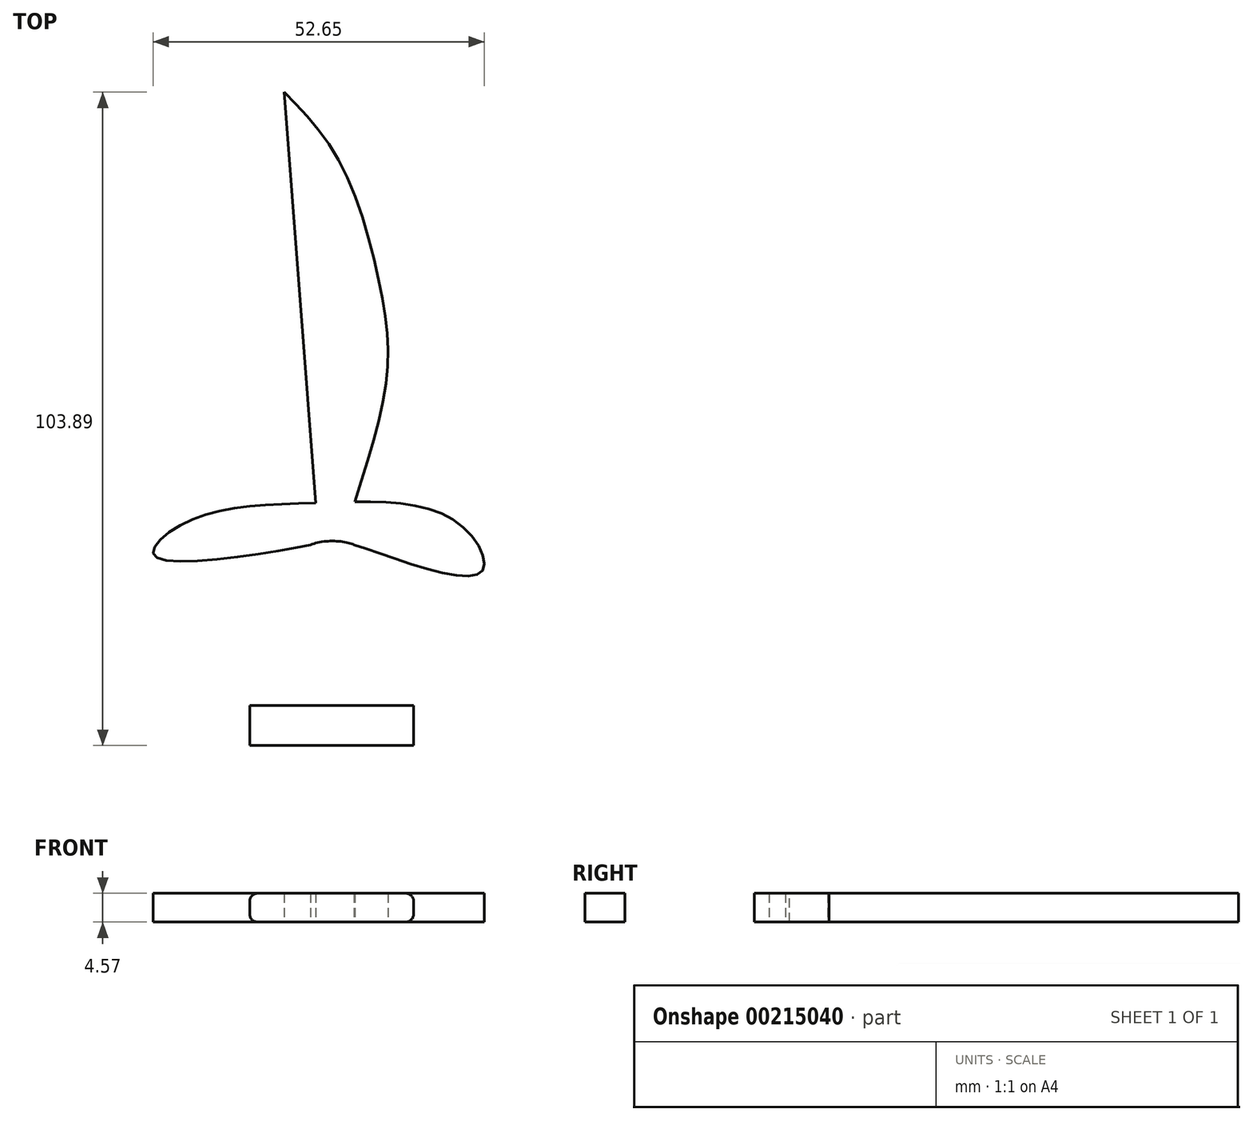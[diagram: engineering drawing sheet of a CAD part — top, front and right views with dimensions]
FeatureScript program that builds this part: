
annotation { "Feature Type Name" : "Feature", "Feature Type Description" : "" }
export const myFeature = defineFeature(function(context is Context, id is Id, definition is map)
    precondition{}
    {
        {
            var Q0;
            Q0=qCreatedBy(makeId("Top.planeOp"),FACE);
            var sketch = newSketch(context, id + "F0", { "sketchPlane" : qUnion([Q0])});
            skFitSpline(sketch, "E0", {"points": [v(-31.24, -28.4) * mm, v(-22.55, -28.4) * mm, v(-21.05, -21.21) * mm, v(-21.38, -5.85) * mm, v(-23.38, -3.34) * mm, v(-29.9, -3.5) * mm, v(-32.57, -9.02) * mm, v(-32.07, -26.22) * mm, v(-31.24, -28.4) * mm]});
            skFitSpline(sketch, "E1", {"points": [v(-29.06, 3.17) * mm, v(-49.94, 0) * mm, v(-54.62, -5.35) * mm, v(-29.9, -3.5) * mm, v(-22.97, -3.5) * mm, v(-3, -8.02) * mm, v(-6.51, 0) * mm, v(-29.06, 3.17) * mm]});
            skLineSegment(sketch, "E2.bottom", {"start": v(-13.53, -29.06) * mm, "end": v(-39.59, -29.06) * mm});
            skLineSegment(sketch, "E2.top", {"start": v(-13.53, -35.41) * mm, "end": v(-39.59, -35.41) * mm});
            skLineSegment(sketch, "E2.left", {"start": v(-13.53, -29.06) * mm, "end": v(-13.53, -35.41) * mm});
            skLineSegment(sketch, "E2.right", {"start": v(-39.59, -29.06) * mm, "end": v(-39.59, -35.41) * mm});
            skPoint(sketch, "E2.middle", {"position": v(-26.56, -32.24) * mm});
            skFitSpline(sketch, "E3", {"points": [v(-22.88, 3.37) * mm, v(-17.87, 22.55) * mm, v(-18.7, 36.75) * mm, v(-25.06, 56.96) * mm, v(-34.08, 68.48) * mm], "startDerivative": vector(24.14, 75.52) * mm, "endDerivative": vector(-42.27, 43.62) * mm});
            skLineSegment(sketch, "E4", {"start": v(-34.08, 68.48) * mm, "end": v(-29.06, 3.17) * mm});
            skSolve(sketch);
        }
        {
            var Q0;
            {var subQ0=sQuery(id+"F0.wireOp",EDGE,"E3");Q0=makeQuery(id+"F0.imprint","IMPRINT",FACE,{"disambiguationData":[TD([[makeQuery(id+"F0.imprint","IMPRINT",EDGE,{"derivedFrom":subQ0}),1.0]])]});}
            var Q1;
            {var subQ0=sQuery(id+"F0.wireOp",EDGE,"E2.bottom");var subQ1=sQuery(id+"F0.wireOp",EDGE,"E0");var subQ2=makeQuery(id+"F0.imprint","INTERSECT",VERTEX,{"disambiguationData":[OD(0.0)],"derivedFrom":[subQ1,subQ0]});Q1=makeQuery(id+"F0.imprint","IMPRINT",FACE,{"disambiguationData":[TD([[makeQuery(id+"F0.imprint","IMPRINT",EDGE,{"disambiguationData":[TD([[subQ2,-1.0]])],"derivedFrom":subQ1}),1.0]])]});}
            var Q2;
            {var subQ0=sQuery(id+"F0.wireOp",EDGE,"E1");var subQ1=sQuery(id+"F0.wireOp",EDGE,"E0");var subQ2=makeQuery(id+"F0.imprint","INTERSECT",VERTEX,{"disambiguationData":[OD(0.0)],"derivedFrom":[subQ1,subQ0]});Q2=makeQuery(id+"F0.imprint","IMPRINT",FACE,{"disambiguationData":[TD([[makeQuery(id+"F0.imprint","IMPRINT",EDGE,{"disambiguationData":[TD([[subQ2,-1.0]])],"derivedFrom":subQ1}),-1.0]])]});}
            var Q3;
            Q3=makeQuery(id+"F0.imprint","IMPRINT",FACE,{"disambiguationData":[TD([[makeQuery(id+"F0.imprint","IMPRINT",EDGE,{"derivedFrom":sQuery(id+"F0.wireOp",EDGE,"E2.top")}),-1.0]])]});
            extrude(context, id + "F1", {"entities" : qUnion([Q0, Q1, Q2, Q3]), "depth" : 4.57 * mm});
        }
        {
            var Q0;
            Q0=makeQuery(id+"F1.opExtrude","CAP_EDGE",EDGE,{"disambiguationData":[OSD([sQuery(id+"F0.wireOp",EDGE,"E2.right")])],"isStart":false});
            fillet(context, id + "F2", {"entities" : qUnion([Q0]), "radius" : 1.27 * mm, "tangentPropagation" : true, "allowEdgeOverflow" : false});
        }
        {
            var Q0;
            Q0=makeQuery(id+"F1.opExtrude","CAP_EDGE",EDGE,{"disambiguationData":[OSD([sQuery(id+"F0.wireOp",EDGE,"E2.right")])],"isStart":true});
            fillet(context, id + "F3", {"entities" : qUnion([Q0]), "radius" : 1.27 * mm, "tangentPropagation" : true, "allowEdgeOverflow" : false});
        }
        {
            var Q0;
            Q0=makeQuery(id+"F1.opExtrude","CAP_EDGE",EDGE,{"disambiguationData":[OSD([sQuery(id+"F0.wireOp",EDGE,"E2.left")])],"isStart":true});
            fillet(context, id + "F4", {"entities" : qUnion([Q0]), "radius" : 1.27 * mm, "tangentPropagation" : true, "allowEdgeOverflow" : false});
        }
        {
            var Q0;
            Q0=makeQuery(id+"F1.opExtrude","CAP_EDGE",EDGE,{"disambiguationData":[OSD([sQuery(id+"F0.wireOp",EDGE,"E2.left")])],"isStart":false});
            fillet(context, id + "F5", {"entities" : qUnion([Q0]), "radius" : 1.27 * mm, "tangentPropagation" : true, "allowEdgeOverflow" : false});
        }
    });
